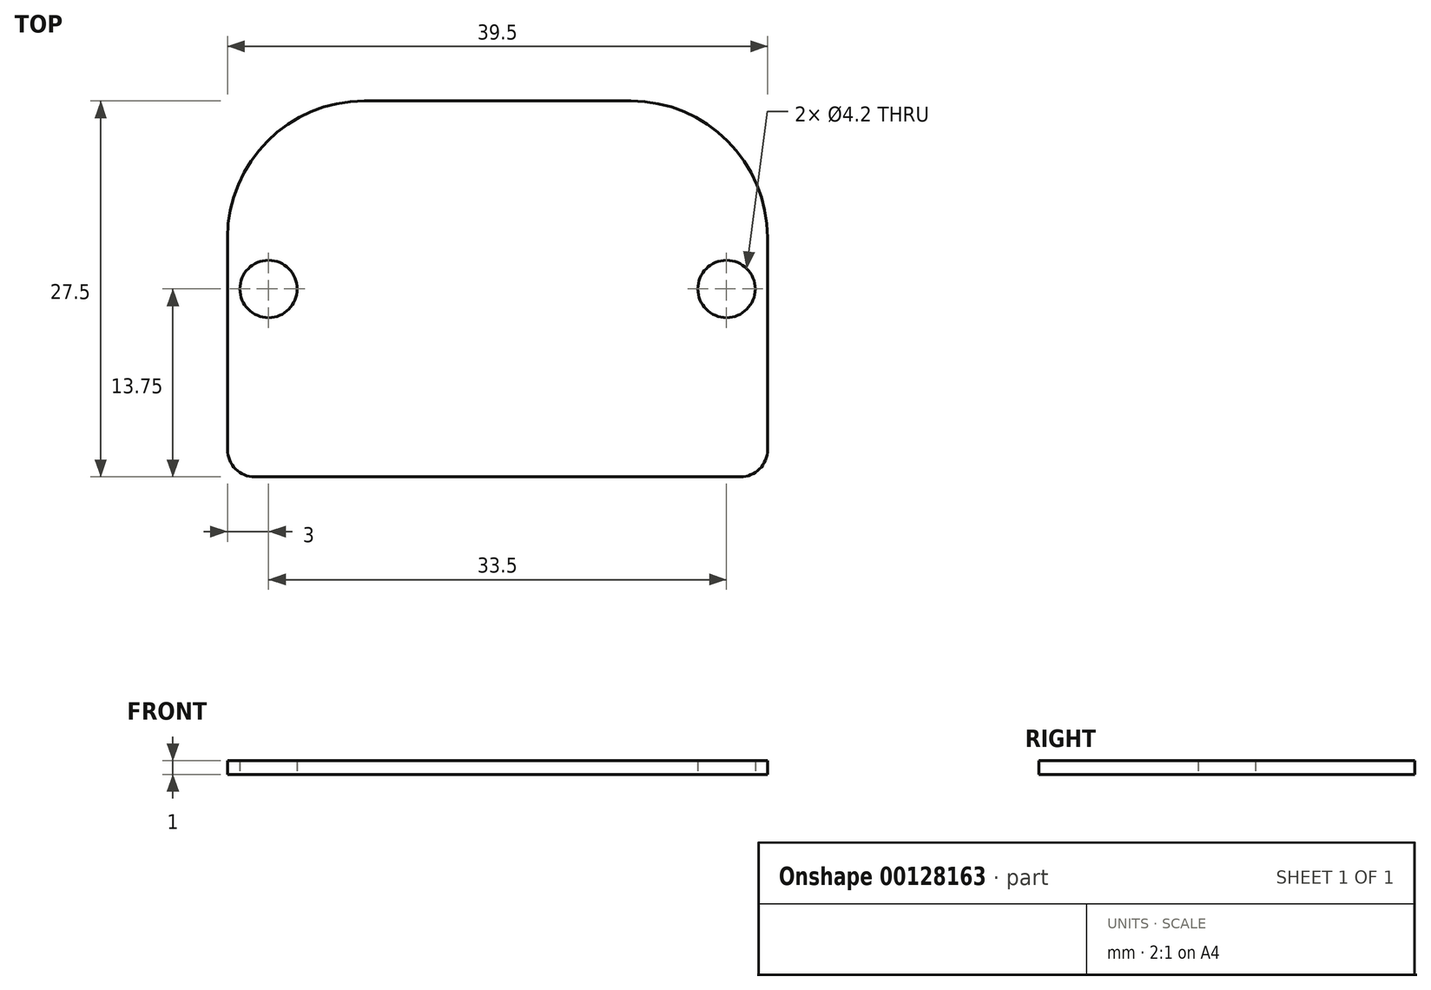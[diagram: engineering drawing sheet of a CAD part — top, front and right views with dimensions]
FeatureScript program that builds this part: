
annotation { "Feature Type Name" : "Feature", "Feature Type Description" : "" }
export const myFeature = defineFeature(function(context is Context, id is Id, definition is map)
    precondition{}
    {
        {
            var Q0;
            Q0=qCreatedBy(makeId("Top.planeOp"),FACE);
            var sketch = newSketch(context, id + "F0", { "sketchPlane" : qUnion([Q0])});
            skLineSegment(sketch, "E0.bottom", {"start": v(-9.75, 13.75) * mm, "end": v(9.75, 13.75) * mm});
            skLineSegment(sketch, "E0.top", {"start": v(-17.75, -13.75) * mm, "end": v(17.75, -13.75) * mm});
            skLineSegment(sketch, "E0.left", {"start": v(-19.75, 3.75) * mm, "end": v(-19.75, -11.75) * mm});
            skLineSegment(sketch, "E0.right", {"start": v(19.75, 3.75) * mm, "end": v(19.75, -11.75) * mm});
            skPoint(sketch, "E1.visualSharp", {"position": v(-19.75, 13.75) * mm});
            skArc(sketch, "E1.filletArc", {"start": v(-9.75, 13.75) * mm, "mid": v(-16.82, 10.82) * mm, "end": v(-19.75, 3.75) * mm});
            skPoint(sketch, "E2.visualSharp", {"position": v(19.75, 13.75) * mm});
            skArc(sketch, "E2.filletArc", {"start": v(19.75, 3.75) * mm, "mid": v(16.82, 10.82) * mm, "end": v(9.75, 13.75) * mm});
            skPoint(sketch, "E3.visualSharp", {"position": v(-19.75, -13.75) * mm});
            skArc(sketch, "E3.filletArc", {"start": v(-19.75, -11.75) * mm, "mid": v(-19.16, -13.16) * mm, "end": v(-17.75, -13.75) * mm});
            skPoint(sketch, "E4.visualSharp", {"position": v(19.75, -13.75) * mm});
            skArc(sketch, "E4.filletArc", {"start": v(17.75, -13.75) * mm, "mid": v(19.16, -13.16) * mm, "end": v(19.75, -11.75) * mm});
            skCircle(sketch, "E5", {"center": v(-16.75, 0) * mm, "radius": 2.1 * mm});
            skCircle(sketch, "E6", {"center": v(16.75, 0) * mm, "radius": 2.1 * mm});
            skSolve(sketch);
        }
        {
            var Q0;
            Q0=makeQuery(id+"F0.imprint","IMPRINT",FACE,{"disambiguationData":[TD([[makeQuery(id+"F0.imprint","IMPRINT",EDGE,{"derivedFrom":sQuery(id+"F0.wireOp",EDGE,"E0.bottom")}),-1.0]])]});
            extrude(context, id + "F1", {"entities" : qUnion([Q0]), "depth" : 1 * mm});
        }
    });
